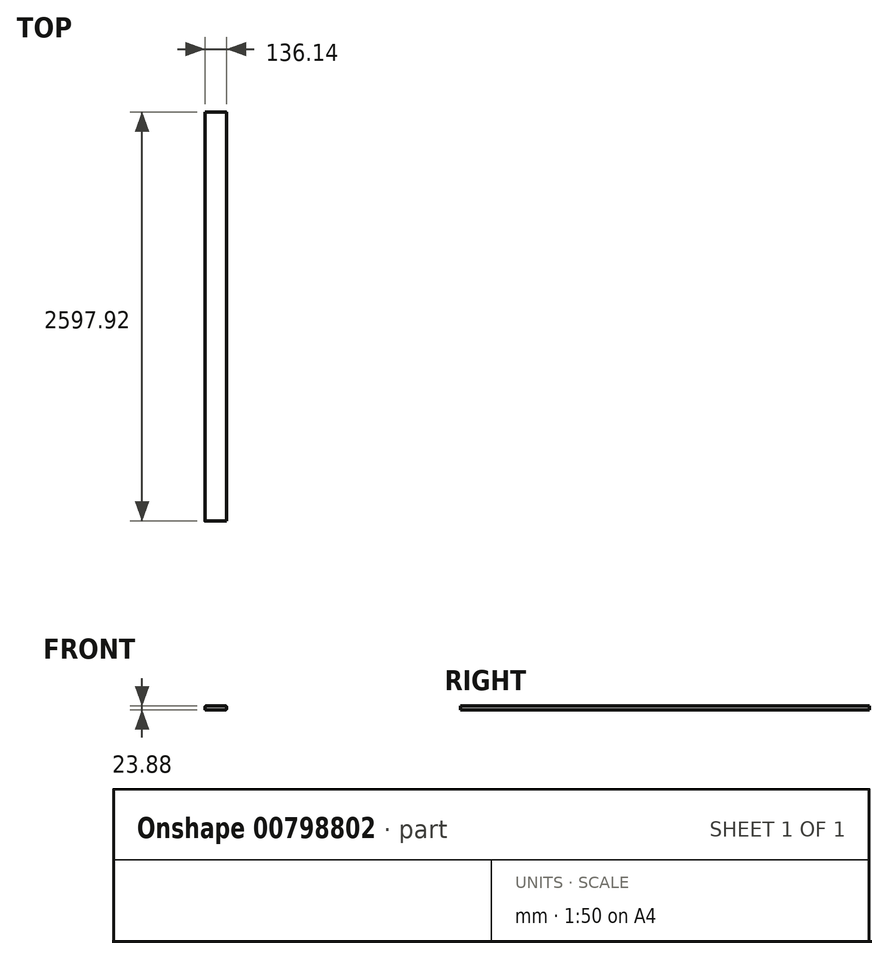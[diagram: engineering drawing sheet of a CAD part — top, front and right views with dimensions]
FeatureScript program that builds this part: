
annotation { "Feature Type Name" : "Feature", "Feature Type Description" : "" }
export const myFeature = defineFeature(function(context is Context, id is Id, definition is map)
    precondition{}
    {
        {
            var Q0;
            Q0=qCreatedBy(makeId("Front.planeOp"),FACE);
            var sketch = newSketch(context, id + "F0", { "sketchPlane" : qUnion([Q0])});
            skLineSegment(sketch, "E0.bottom", {"start": v(-63.25, 11.94) * mm, "end": v(63.25, 11.94) * mm});
            skLineSegment(sketch, "E0.top", {"start": v(-63.25, -11.94) * mm, "end": v(63.25, -11.94) * mm});
            skLineSegment(sketch, "E0.left", {"start": v(-68.07, 7.11) * mm, "end": v(-68.07, -7.11) * mm});
            skLineSegment(sketch, "E0.right", {"start": v(68.07, 7.11) * mm, "end": v(68.07, -7.11) * mm});
            skPoint(sketch, "E0.middle", {"position": v(0, 0) * mm});
            skPoint(sketch, "E1.visualSharp", {"position": v(-68.07, 11.94) * mm});
            skArc(sketch, "E1.filletArc", {"start": v(-63.25, 11.94) * mm, "mid": v(-66.66, 10.52) * mm, "end": v(-68.07, 7.11) * mm});
            skPoint(sketch, "E2.visualSharp", {"position": v(68.07, 11.94) * mm});
            skArc(sketch, "E2.filletArc", {"start": v(68.07, 7.11) * mm, "mid": v(66.66, 10.52) * mm, "end": v(63.25, 11.94) * mm});
            skPoint(sketch, "E3.visualSharp", {"position": v(68.07, -11.94) * mm});
            skArc(sketch, "E3.filletArc", {"start": v(63.25, -11.94) * mm, "mid": v(66.66, -10.52) * mm, "end": v(68.07, -7.11) * mm});
            skPoint(sketch, "E4.visualSharp", {"position": v(-68.07, -11.94) * mm});
            skArc(sketch, "E4.filletArc", {"start": v(-68.07, -7.11) * mm, "mid": v(-66.66, -10.52) * mm, "end": v(-63.25, -11.94) * mm});
            skSolve(sketch);
        }
        {
            var Q0;
            Q0=makeQuery(id+"F0.imprint","IMPRINT",FACE,{"disambiguationData":[TD([[makeQuery(id+"F0.imprint","IMPRINT",EDGE,{"derivedFrom":sQuery(id+"F0.wireOp",EDGE,"E0.bottom")}),-1.0]])]});
            extrude(context, id + "F1", {"entities" : qUnion([Q0]), "endBound" : BoundingType.SYMMETRIC, "depth" : 2597.9 * mm, "offsetDistance" : 25.4 * mm});
        }
    });
